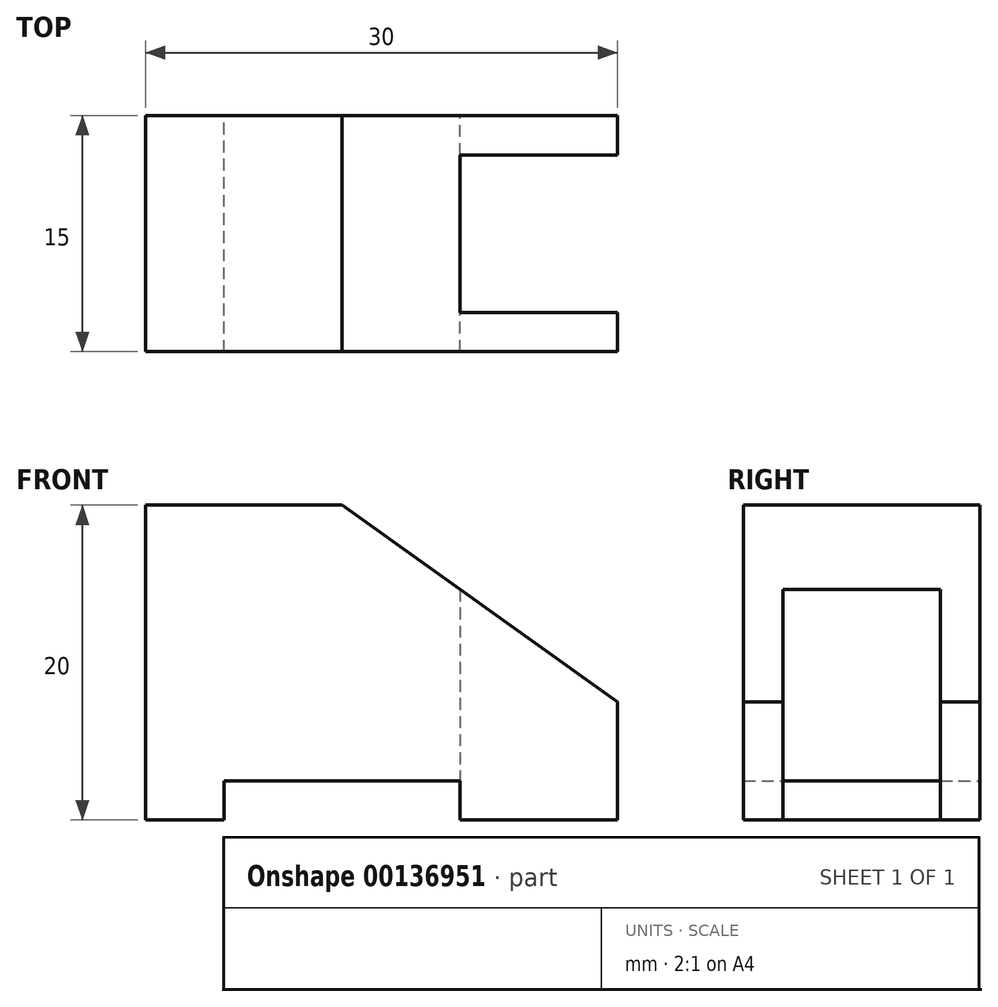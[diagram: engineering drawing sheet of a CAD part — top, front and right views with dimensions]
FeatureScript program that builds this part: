
annotation { "Feature Type Name" : "Feature", "Feature Type Description" : "" }
export const myFeature = defineFeature(function(context is Context, id is Id, definition is map)
    precondition{}
    {
        {
            var Q0;
            Q0=qCreatedBy(makeId("Front.planeOp"),FACE);
            var sketch = newSketch(context, id + "F0", { "sketchPlane" : qUnion([Q0])});
            skLineSegment(sketch, "E0.bottom", {"start": v(0, 0) * mm, "end": v(30, 0) * mm});
            skLineSegment(sketch, "E0.top", {"start": v(0, 20) * mm, "end": v(30, 20) * mm});
            skLineSegment(sketch, "E0.left", {"start": v(0, 0) * mm, "end": v(0, 20) * mm});
            skLineSegment(sketch, "E0.right", {"start": v(30, 0) * mm, "end": v(30, 20) * mm});
            skLineSegment(sketch, "E1.bottom", {"start": v(5, 0) * mm, "end": v(20, 0) * mm});
            skLineSegment(sketch, "E1.top", {"start": v(5, 2.5) * mm, "end": v(20, 2.5) * mm});
            skLineSegment(sketch, "E1.left", {"start": v(5, 0) * mm, "end": v(5, 2.5) * mm});
            skLineSegment(sketch, "E1.right", {"start": v(20, 0) * mm, "end": v(20, 2.5) * mm});
            skLineSegment(sketch, "E2", {"start": v(12.5, 20) * mm, "end": v(30, 7.5) * mm});
            skSolve(sketch);
        }
        {
            var Q0;
            {var subQ0=sQuery(id+"F0.wireOp",EDGE,"E0.left");Q0=makeQuery(id+"F0.imprint","IMPRINT",FACE,{"disambiguationData":[TD([[makeQuery(id+"F0.imprint","IMPRINT",EDGE,{"derivedFrom":subQ0}),-1.0]])]});}
            extrude(context, id + "F1", {"entities" : qUnion([Q0]), "depth" : 15 * mm});
        }
        {
            var Q0;
            {var subQ0=sQuery(id+"F0.wireOp",EDGE,"E0.bottom");Q0=makeQuery(id+"F1.opExtrude","SWEPT_FACE",FACE,{"disambiguationData":[OSD([subQ0]),TDD([makeQuery(id+"F0.imprint","IMPRINT",EDGE,{"disambiguationData":[TD([[makeQuery(id+"F0.imprint","INTERSECT",VERTEX,{"derivedFrom":[subQ0,sQuery(id+"F0.wireOp",EDGE,"E0.right")]}),1.0]])],"derivedFrom":subQ0})])]});}
            var sketch = newSketch(context, id + "F2", { "sketchPlane" : qUnion([Q0])});
            skLineSegment(sketch, "E3.bottom", {"start": v(30, 12.5) * mm, "end": v(20, 12.5) * mm});
            skLineSegment(sketch, "E3.top", {"start": v(30, 2.5) * mm, "end": v(20, 2.5) * mm});
            skLineSegment(sketch, "E3.left", {"start": v(30, 12.5) * mm, "end": v(30, 2.5) * mm});
            skLineSegment(sketch, "E3.right", {"start": v(20, 12.5) * mm, "end": v(20, 2.5) * mm});
            skSolve(sketch);
        }
        {
            var Q0;
            Q0 = qSketchRegion(id + "F2", true);
            extrude(context, id + "F3", {"entities" : qUnion([Q0]), "operationType" : NewBodyOperationType.REMOVE, "endBound" : BoundingType.THROUGH_ALL, "oppositeDirection" : true, "depth" : 25 * mm});
        }
    });
